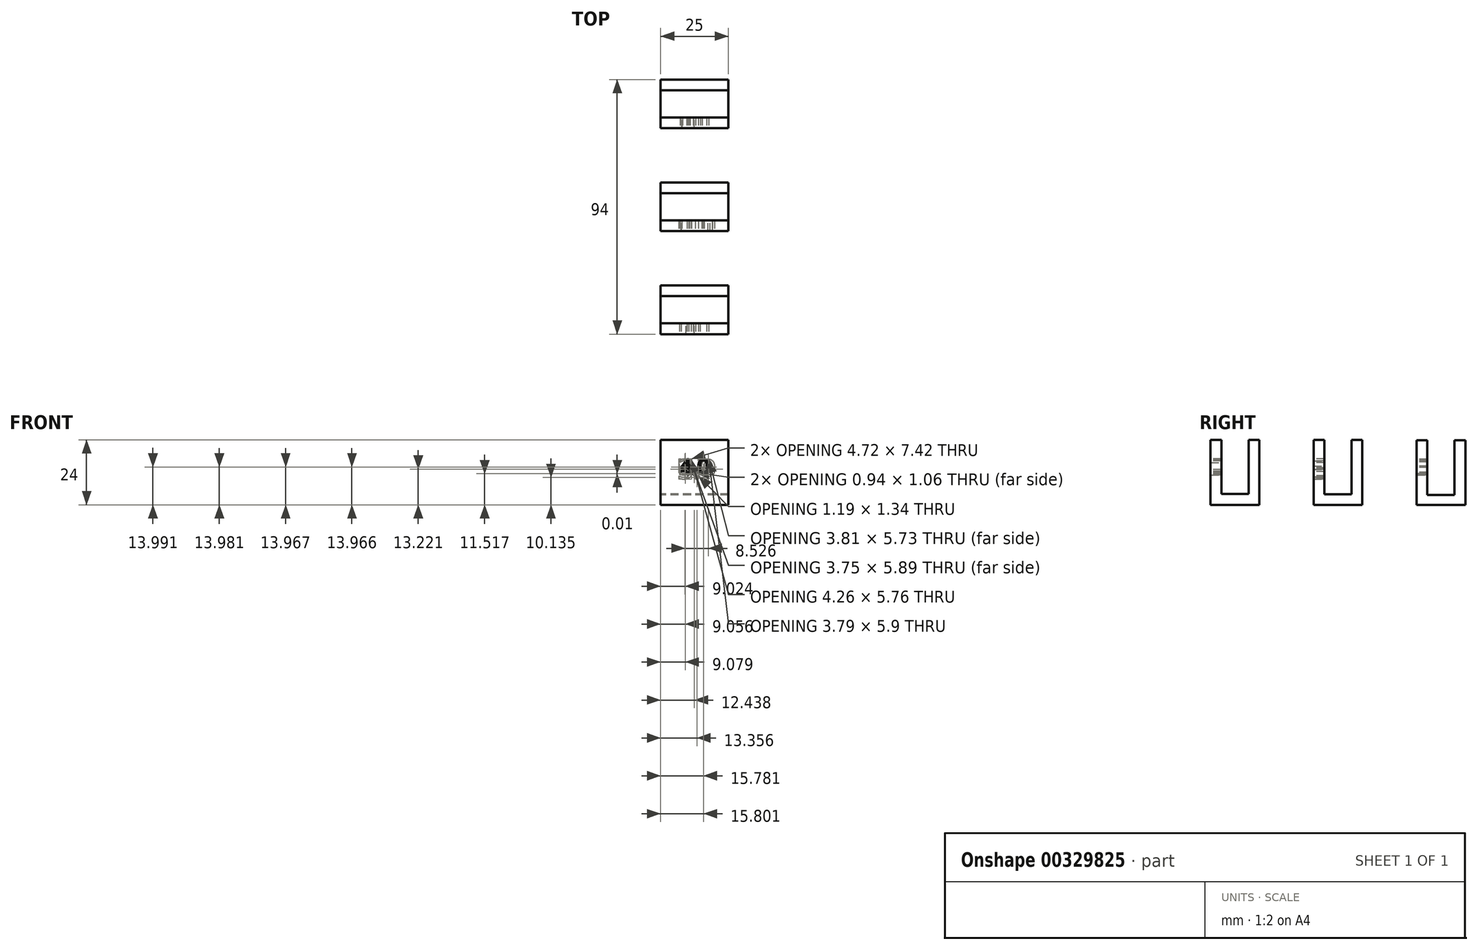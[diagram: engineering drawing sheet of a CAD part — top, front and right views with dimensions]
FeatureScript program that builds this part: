
annotation { "Feature Type Name" : "Feature", "Feature Type Description" : "" }
export const myFeature = defineFeature(function(context is Context, id is Id, definition is map)
    precondition{}
    {
        {
            var Q0;
            Q0=qCreatedBy(makeId("Right.planeOp"),FACE);
            var sketch = newSketch(context, id + "F0", { "sketchPlane" : qUnion([Q0])});
            skLineSegment(sketch, "E0", {"start": v(-38, 0) * mm, "end": v(-38, 24) * mm});
            skLineSegment(sketch, "E1", {"start": v(-38, 24) * mm, "end": v(-42, 24) * mm});
            skLineSegment(sketch, "E2", {"start": v(-42, 24) * mm, "end": v(-42, 4) * mm});
            skLineSegment(sketch, "E3", {"start": v(-42, 4) * mm, "end": v(-47, 4) * mm});
            skLineSegment(sketch, "E4", {"start": v(-47, 4) * mm, "end": v(-47, 0) * mm, "construction": true});
            skLineSegment(sketch, "E5", {"start": v(-47, 0) * mm, "end": v(-38, 0) * mm});
            skLineSegment(sketch, "E6.MirrorCS", {"start": v(-52, 4) * mm, "end": v(-47, 4) * mm});
            skLineSegment(sketch, "E7.MirrorCS", {"start": v(-52, 24) * mm, "end": v(-52, 4) * mm});
            skLineSegment(sketch, "E8.MirrorCS", {"start": v(-56, 24) * mm, "end": v(-52, 24) * mm});
            skLineSegment(sketch, "E9.MirrorCS", {"start": v(-56, 0) * mm, "end": v(-56, 24) * mm});
            skLineSegment(sketch, "E10.MirrorCS", {"start": v(-47, 0) * mm, "end": v(-56, 0) * mm});
            skLineSegment(sketch, "E11", {"start": v(-9, 0) * mm, "end": v(-9, 3.9) * mm, "construction": true});
            skLineSegment(sketch, "E12", {"start": v(-9, 3.9) * mm, "end": v(-4, 3.9) * mm});
            skLineSegment(sketch, "E13", {"start": v(-4, 3.9) * mm, "end": v(-4, 24) * mm});
            skLineSegment(sketch, "E14", {"start": v(-4, 24) * mm, "end": v(0, 24) * mm});
            skLineSegment(sketch, "E15", {"start": v(0, 24) * mm, "end": v(0, 0) * mm});
            skLineSegment(sketch, "E16", {"start": v(0, 0) * mm, "end": v(-9, 0) * mm});
            skLineSegment(sketch, "E17.MirrorCS", {"start": v(-9, 3.9) * mm, "end": v(-14, 3.9) * mm});
            skLineSegment(sketch, "E18.MirrorCS", {"start": v(-14, 3.9) * mm, "end": v(-14, 24) * mm});
            skLineSegment(sketch, "E19.MirrorCS", {"start": v(-14, 24) * mm, "end": v(-18, 24) * mm});
            skLineSegment(sketch, "E20.MirrorCS", {"start": v(-18, 24) * mm, "end": v(-18, 0) * mm});
            skLineSegment(sketch, "E21.MirrorCS", {"start": v(-18, 0) * mm, "end": v(-9, 0) * mm});
            skLineSegment(sketch, "E22", {"start": v(29, 0) * mm, "end": v(38, 0) * mm});
            skLineSegment(sketch, "E23", {"start": v(38, 0) * mm, "end": v(38, 23.8) * mm});
            skLineSegment(sketch, "E24", {"start": v(38, 23.8) * mm, "end": v(34, 23.8) * mm});
            skLineSegment(sketch, "E25", {"start": v(34, 23.8) * mm, "end": v(34, 3.7) * mm});
            skLineSegment(sketch, "E26", {"start": v(34, 3.7) * mm, "end": v(29, 3.7) * mm});
            skLineSegment(sketch, "E27", {"start": v(29, 3.7) * mm, "end": v(29, 0) * mm, "construction": true});
            skLineSegment(sketch, "E28.MirrorCS", {"start": v(24, 3.7) * mm, "end": v(29, 3.7) * mm});
            skLineSegment(sketch, "E29.MirrorCS", {"start": v(24, 23.8) * mm, "end": v(24, 3.7) * mm});
            skLineSegment(sketch, "E30.MirrorCS", {"start": v(20, 23.8) * mm, "end": v(24, 23.8) * mm});
            skLineSegment(sketch, "E31.MirrorCS", {"start": v(20, 0) * mm, "end": v(20, 23.8) * mm});
            skLineSegment(sketch, "E32.MirrorCS", {"start": v(29, 0) * mm, "end": v(20, 0) * mm});
            skSolve(sketch);
        }
        {
            var Q0;
            Q0 = qSketchRegion(id + "F0", true);
            extrude(context, id + "F1", {"entities" : qUnion([Q0]), "depth" : 25 * mm});
        }
        {
            var Q0;
            Q0=makeQuery(id+"F1.opExtrude","SWEPT_FACE",FACE,{"disambiguationData":[OSD([sQuery(id+"F0.wireOp",EDGE,"E9.MirrorCS")])]});
            var sketch = newSketch(context, id + "F2", { "sketchPlane" : qUnion([Q0])});
            skText(sketch, "E33", { "text": "4.0", "fontName": "OpenSans-Regular.ttf"});
            skLineSegment(sketch, "E34", {"start": v(6.78, 14) * mm, "end": v(0, 14) * mm, "construction": true});
            skPoint(sketch, "E34.endSnap0", {"position": v(6.78, 14) * mm});
            skLineSegment(sketch, "E35", {"start": v(0, 24) * mm, "end": v(0, 14) * mm, "construction": true});
            skLineSegment(sketch, "E36", {"start": v(0, 14) * mm, "end": v(0, 4) * mm, "construction": true});
            const initialGuessF2  = {"E33": [0.00678, 0.01111, 1, 0, 0.00578]};
            skSetInitialGuess(sketch, initialGuessF2);
            skSolve(sketch);
        }
        {
            var Q0;
            Q0=makeQuery(id+"F1.opExtrude","SWEPT_FACE",FACE,{"disambiguationData":[OSD([sQuery(id+"F0.wireOp",EDGE,"E20.MirrorCS")])]});
            var sketch = newSketch(context, id + "F3", { "sketchPlane" : qUnion([Q0])});
            skText(sketch, "E37", { "text": "3.9", "fontName": "OpenSans-Regular.ttf"});
            const initialGuessF3  = {"E37": [0.00623, 0.00961, 1, 0, 0.00728]};
            skSetInitialGuess(sketch, initialGuessF3);
            skSolve(sketch);
        }
        {
            var Q0;
            Q0=makeQuery(id+"F1.opExtrude","SWEPT_FACE",FACE,{"disambiguationData":[OSD([sQuery(id+"F0.wireOp",EDGE,"E31.MirrorCS")])]});
            var sketch = newSketch(context, id + "F4", { "sketchPlane" : qUnion([Q0])});
            skText(sketch, "E38", { "text": "3.7", "fontName": "OpenSans-Regular.ttf"});
            const initialGuessF4  = {"E38": [0.00678, 0.0111, 1, 0, 0.00578]};
            skSetInitialGuess(sketch, initialGuessF4);
            skSolve(sketch);
        }
        {
            var Q0;
            Q0 = qSketchRegion(id + "F2", true);
            extrude(context, id + "F5", {"entities" : qUnion([Q0]), "operationType" : NewBodyOperationType.REMOVE, "endBound" : BoundingType.UP_TO_NEXT, "oppositeDirection" : true, "depth" : 25 * mm});
        }
        {
            var Q0;
            Q0 = qSketchRegion(id + "F3", true);
            extrude(context, id + "F6", {"entities" : qUnion([Q0]), "operationType" : NewBodyOperationType.REMOVE, "endBound" : BoundingType.UP_TO_NEXT, "oppositeDirection" : true, "depth" : 25 * mm});
        }
        {
            var Q0;
            Q0 = qSketchRegion(id + "F4", true);
            extrude(context, id + "F7", {"entities" : qUnion([Q0]), "operationType" : NewBodyOperationType.REMOVE, "endBound" : BoundingType.UP_TO_NEXT, "oppositeDirection" : true, "depth" : 25 * mm});
        }
    });
